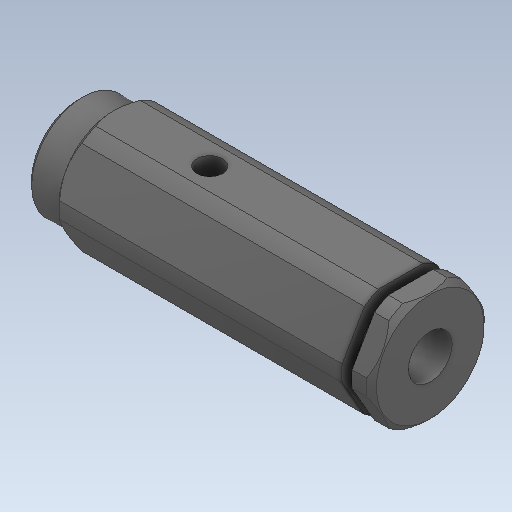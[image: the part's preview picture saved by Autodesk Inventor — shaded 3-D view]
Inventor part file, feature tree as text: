
AUTODESK INVENTOR PART (.ipt)
format: ipt  version: 2020 (Build 240168000, 168)  size: 166,400 bytes
history: native  units: in
note: dims shown in document units (in); Inventor stores cm internally (conversion verified against a paired STEP export)
features: chamfer x1
ambient origin geometry x8: Origin, YZ Plane, XZ Plane, XY Plane, X Axis, Y Axis, Z Axis, Center Point
bodies: Solid1 (feature_tree)
feature tree (1):
  chamfer  "Chamfer1"  [1 undecoded]
note: 1 required parameter value undecoded (feature->parameter linkage not recoverable at this tier; creation-order binding heuristic only, values carry confidence <= 0.55)
